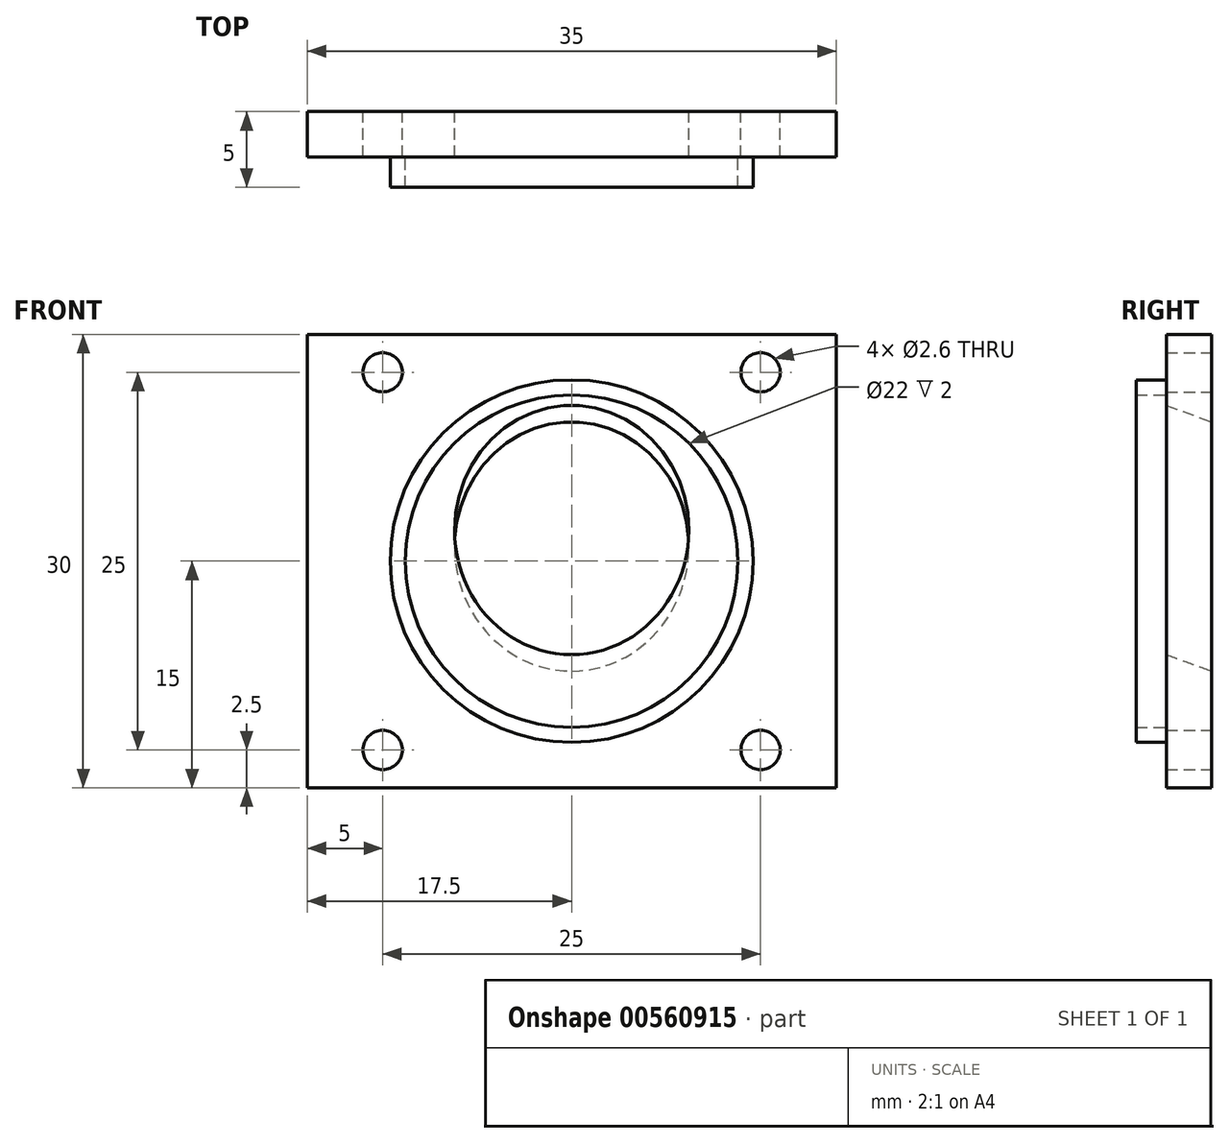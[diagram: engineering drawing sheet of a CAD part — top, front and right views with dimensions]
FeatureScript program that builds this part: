
annotation { "Feature Type Name" : "Feature", "Feature Type Description" : "" }
export const myFeature = defineFeature(function(context is Context, id is Id, definition is map)
    precondition{}
    {
        {
            var Q0;
            Q0=qCreatedBy(makeId("Front.planeOp"),FACE);
            var sketch = newSketch(context, id + "F0", { "sketchPlane" : qUnion([Q0])});
            skLineSegment(sketch, "E0.bottom", {"start": v(-17.5, 15) * mm, "end": v(17.5, 15) * mm});
            skLineSegment(sketch, "E0.top", {"start": v(-17.5, -15) * mm, "end": v(17.5, -15) * mm});
            skLineSegment(sketch, "E0.left", {"start": v(-17.5, 15) * mm, "end": v(-17.5, -15) * mm});
            skLineSegment(sketch, "E0.right", {"start": v(17.5, 15) * mm, "end": v(17.5, -15) * mm});
            skCircle(sketch, "E1", {"center": v(-12.5, 12.5) * mm, "radius": 1.3 * mm});
            skCircle(sketch, "E2", {"center": v(12.5, 12.5) * mm, "radius": 1.3 * mm});
            skCircle(sketch, "E3", {"center": v(12.5, -12.5) * mm, "radius": 1.3 * mm});
            skCircle(sketch, "E4", {"center": v(-12.5, -12.5) * mm, "radius": 1.3 * mm});
            skCircle(sketch, "E5", {"center": v(0, 0) * mm, "radius": 12 * mm});
            skCircle(sketch, "E6", {"center": v(0, 0) * mm, "radius": 11 * mm});
            skSolve(sketch);
        }
        {
            var Q0;
            Q0=makeQuery(id+"F0.imprint","IMPRINT",FACE,{"disambiguationData":[TD([[makeQuery(id+"F0.imprint","IMPRINT",EDGE,{"derivedFrom":sQuery(id+"F0.wireOp",EDGE,"E0.bottom")}),-1.0]])]});
            var Q1;
            Q1=makeQuery(id+"F0.imprint","IMPRINT",FACE,{"disambiguationData":[TD([[makeQuery(id+"F0.imprint","IMPRINT",EDGE,{"derivedFrom":sQuery(id+"F0.wireOp",EDGE,"E6")}),1.0]])]});
            var Q2;
            Q2=makeQuery(id+"F0.imprint","IMPRINT",FACE,{"disambiguationData":[TD([[makeQuery(id+"F0.imprint","IMPRINT",EDGE,{"derivedFrom":sQuery(id+"F0.wireOp",EDGE,"E5")}),1.0]])]});
            extrude(context, id + "F1", {"entities" : qUnion([Q0, Q1, Q2]), "depth" : 3 * mm, "offsetDistance" : 25 * mm});
        }
        {
            var Q0;
            Q0=qCreatedBy(makeId("Right.planeOp"),FACE);
            var sketch = newSketch(context, id + "F2", { "sketchPlane" : qUnion([Q0])});
            skLineSegment(sketch, "E7", {"start": v(30.06, -1.73) * mm, "end": v(-14.7, 14.57) * mm});
            skLineSegment(sketch, "E8", {"start": v(-14.7, 14.57) * mm, "end": v(-20, 0) * mm});
            skLineSegment(sketch, "E9", {"start": v(-20, 0) * mm, "end": v(24.76, -16.3) * mm});
            skLineSegment(sketch, "E10", {"start": v(24.76, -16.3) * mm, "end": v(30.06, -1.73) * mm});
            skSolve(sketch);
        }
        {
            var Q0;
            Q0=makeQuery(id+"F2.imprint","IMPRINT",FACE,{"disambiguationData":[TD([[makeQuery(id+"F2.imprint","IMPRINT",EDGE,{"derivedFrom":sQuery(id+"F2.wireOp",EDGE,"E7")}),1.0]])]});
            extrude(context, id + "F3", {"entities" : qUnion([Q0]), "operationType" : NewBodyOperationType.REMOVE, "depth" : 15.5 * mm, "offsetDistance" : 25 * mm, "symmetric" : true});
        }
        {
            var Q0;
            Q0=makeQuery(id+"F3.boolean.opBoolean","COPY",EDGE,{"derivedFrom":makeQuery(id+"F3.opExtrude","CAP_EDGE",EDGE,{"disambiguationData":[OSD([sQuery(id+"F2.wireOp",EDGE,"E7")])],"isStart":false})});
            var Q1;
            Q1=makeQuery(id+"F3.boolean.opBoolean","COPY",EDGE,{"derivedFrom":makeQuery(id+"F3.opExtrude","CAP_EDGE",EDGE,{"disambiguationData":[OSD([sQuery(id+"F2.wireOp",EDGE,"E7")])],"isStart":true})});
            var Q2;
            Q2=makeQuery(id+"F3.boolean.opBoolean","COPY",EDGE,{"derivedFrom":makeQuery(id+"F3.opExtrude","CAP_EDGE",EDGE,{"disambiguationData":[OSD([sQuery(id+"F2.wireOp",EDGE,"E9")])],"isStart":true})});
            var Q3;
            Q3=makeQuery(id+"F3.boolean.opBoolean","COPY",EDGE,{"derivedFrom":makeQuery(id+"F3.opExtrude","CAP_EDGE",EDGE,{"disambiguationData":[OSD([sQuery(id+"F2.wireOp",EDGE,"E9")])],"isStart":false})});
            fillet(context, id + "F4", {"entities" : qUnion([Q0, Q1, Q2, Q3]), "radius" : 7.75 * mm, "tangentPropagation" : true, "allowEdgeOverflow" : false});
        }
        {
            var Q0;
            Q0=makeQuery(id+"F0.imprint","IMPRINT",FACE,{"disambiguationData":[TD([[makeQuery(id+"F0.imprint","IMPRINT",EDGE,{"derivedFrom":sQuery(id+"F0.wireOp",EDGE,"E5")}),1.0]])]});
            extrude(context, id + "F5", {"entities" : qUnion([Q0]), "operationType" : NewBodyOperationType.ADD, "depth" : 5 * mm, "offsetDistance" : 25 * mm});
        }
    });
